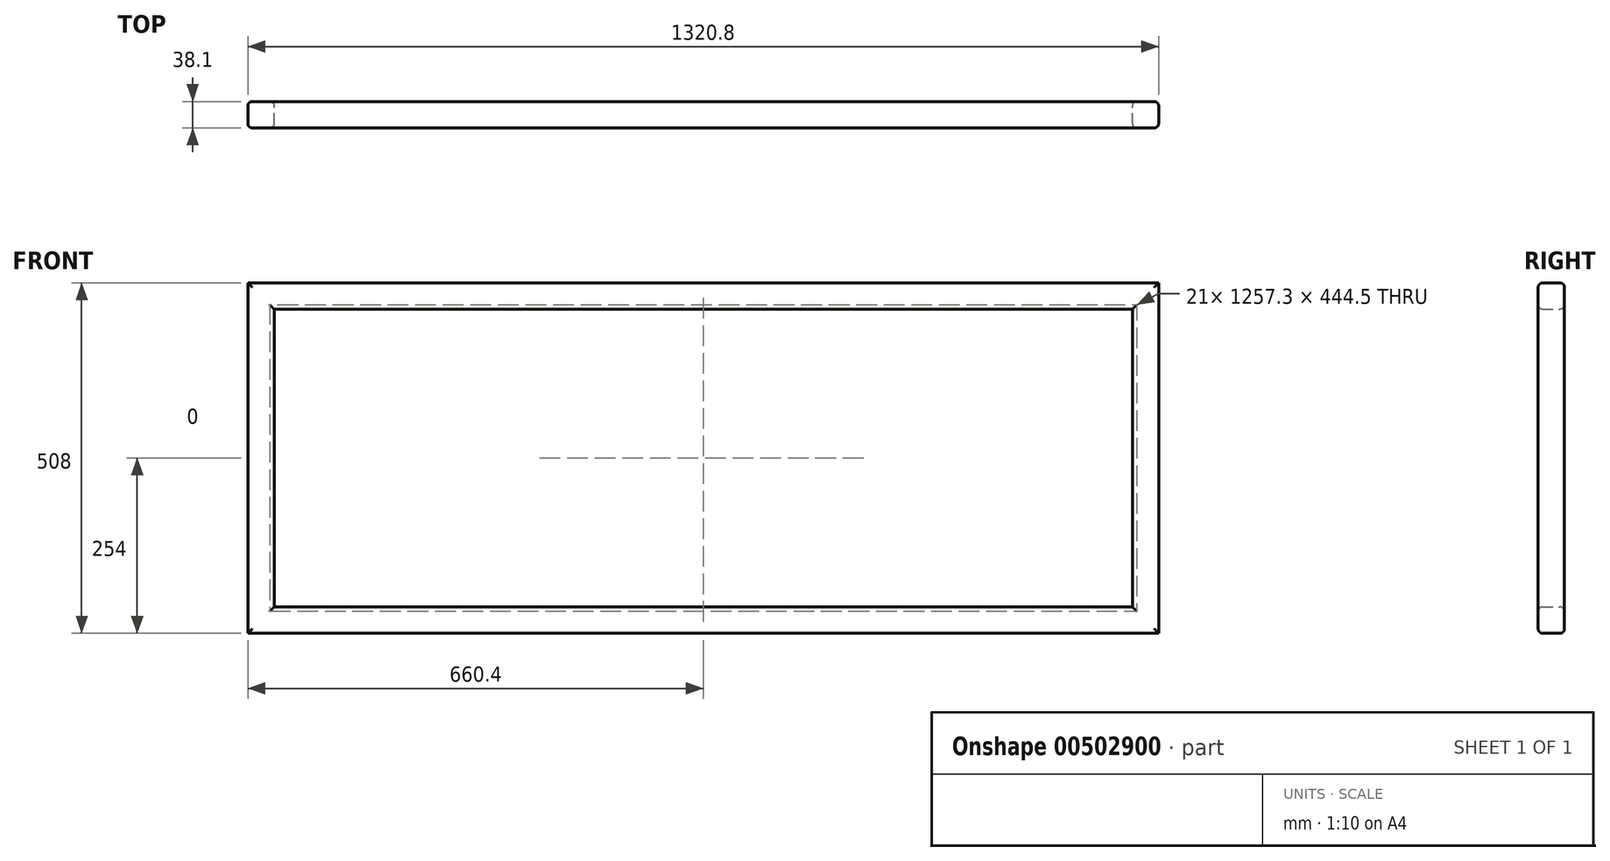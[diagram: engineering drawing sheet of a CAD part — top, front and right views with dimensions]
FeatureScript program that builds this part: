
annotation { "Feature Type Name" : "Feature", "Feature Type Description" : "" }
export const myFeature = defineFeature(function(context is Context, id is Id, definition is map)
    precondition{}
    {
        {
            var Q0;
            Q0=qCreatedBy(makeId("Front.planeOp"),FACE);
            var sketch = newSketch(context, id + "F0", { "sketchPlane" : qUnion([Q0])});
            skLineSegment(sketch, "E0", {"start": v(0, 0) * mm, "end": v(-660.4, 0) * mm});
            skLineSegment(sketch, "E1", {"start": v(-660.4, 0) * mm, "end": v(-660.4, 508) * mm});
            skLineSegment(sketch, "E2", {"start": v(-660.4, 508) * mm, "end": v(660.4, 508) * mm});
            skLineSegment(sketch, "E3", {"start": v(660.4, 508) * mm, "end": v(660.4, 0) * mm});
            skLineSegment(sketch, "E4", {"start": v(660.4, 0) * mm, "end": v(0, 0) * mm});
            skSolve(sketch);
        }
        {
            var Q0;
            Q0=qCreatedBy(makeId("Right.planeOp"),FACE);
            var sketch = newSketch(context, id + "F1", { "sketchPlane" : qUnion([Q0])});
            skLineSegment(sketch, "E5", {"start": v(0, 0) * mm, "end": v(-12.7, 0) * mm});
            skLineSegment(sketch, "E6", {"start": v(-19.05, 6.35) * mm, "end": v(-19.05, 31.75) * mm});
            skLineSegment(sketch, "E7", {"start": v(-12.7, 38.1) * mm, "end": v(12.7, 38.1) * mm});
            skLineSegment(sketch, "E8", {"start": v(19.05, 31.75) * mm, "end": v(19.05, 6.35) * mm});
            skLineSegment(sketch, "E9", {"start": v(12.7, 0) * mm, "end": v(0, 0) * mm});
            skPoint(sketch, "E10.visualSharp", {"position": v(-19.05, 0) * mm});
            skArc(sketch, "E10.filletArc", {"start": v(-19.05, 6.35) * mm, "mid": v(-17.2, 1.86) * mm, "end": v(-12.7, 0) * mm});
            skPoint(sketch, "E11.visualSharp", {"position": v(-19.05, 38.1) * mm});
            skArc(sketch, "E11.filletArc", {"start": v(-12.7, 38.1) * mm, "mid": v(-17.2, 36.24) * mm, "end": v(-19.05, 31.75) * mm});
            skPoint(sketch, "E12.visualSharp", {"position": v(19.05, 38.1) * mm});
            skArc(sketch, "E12.filletArc", {"start": v(19.05, 31.75) * mm, "mid": v(17.2, 36.24) * mm, "end": v(12.7, 38.1) * mm});
            skPoint(sketch, "E13.visualSharp", {"position": v(19.05, 0) * mm});
            skArc(sketch, "E13.filletArc", {"start": v(12.7, 0) * mm, "mid": v(17.2, 1.86) * mm, "end": v(19.05, 6.35) * mm});
            skSolve(sketch);
        }
        {
            var Q0;
            Q0=makeQuery(id+"F1.imprint","IMPRINT",FACE,{"disambiguationData":[TD([[makeQuery(id+"F1.imprint","IMPRINT",EDGE,{"derivedFrom":sQuery(id+"F1.wireOp",EDGE,"E5")}),-1.0]])]});
            var Q1;
            Q1=sQuery(id+"F0.wireOp",EDGE,"E4");
            var Q2;
            Q2=sQuery(id+"F0.wireOp",EDGE,"E3");
            var Q3;
            Q3=sQuery(id+"F0.wireOp",EDGE,"E2");
            var Q4;
            Q4=sQuery(id+"F0.wireOp",EDGE,"E1");
            var Q5;
            Q5=sQuery(id+"F0.wireOp",EDGE,"E0");
            sweep(context, id + "F2", {"profiles" : qUnion([Q0]), "path" : qUnion([Q1, Q2, Q3, Q4, Q5])});
        }
    });
